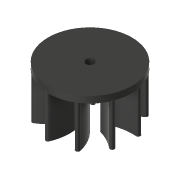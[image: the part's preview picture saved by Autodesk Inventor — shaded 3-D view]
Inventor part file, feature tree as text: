
AUTODESK INVENTOR PART (.ipt)
format: ipt  version: 2017 (Build 210142000, 142)  size: 186,368 bytes
history: native  units: in
note: dims shown in document units (in); Inventor stores cm internally (conversion verified against a paired STEP export)
features: extrude x3, sketch x3, pattern_circular x1, chamfer x1
ambient origin geometry x8: Origin, YZ Plane, XZ Plane, XY Plane, X Axis, Y Axis, Z Axis, Center Point
bodies: Solid1 (feature_tree)
feature tree (8):
  extrude  "Extrusion1"  Depth=0.0787in
  extrude  "Extrusion2"  Depth=0.2in
  extrude  "Extrusion3"  Depth=0.0394in
  pattern_circular  "Circular Pattern1"  [2 undecoded]
  chamfer  "Chamfer1"  Distance=3.937in Angle=360.0deg
  sketch  "Sketch1"  dims[d0=0.7874in d1=0.0787in]
  sketch  "Sketch2"  dims[d2=0.0625in d3=0.0in d4=0.2in]
  sketch  "Sketch3"  dims[d5=0.2in d6=0.0in d7=0.0394in d8=0.4in d9=0.0in d10=3.937in d11=360.0deg d13=0.05in d14=0.125in d15=45.0deg]
note: 2 required parameter values undecoded (feature->parameter linkage not recoverable at this tier; creation-order binding heuristic only, values carry confidence <= 0.55)
